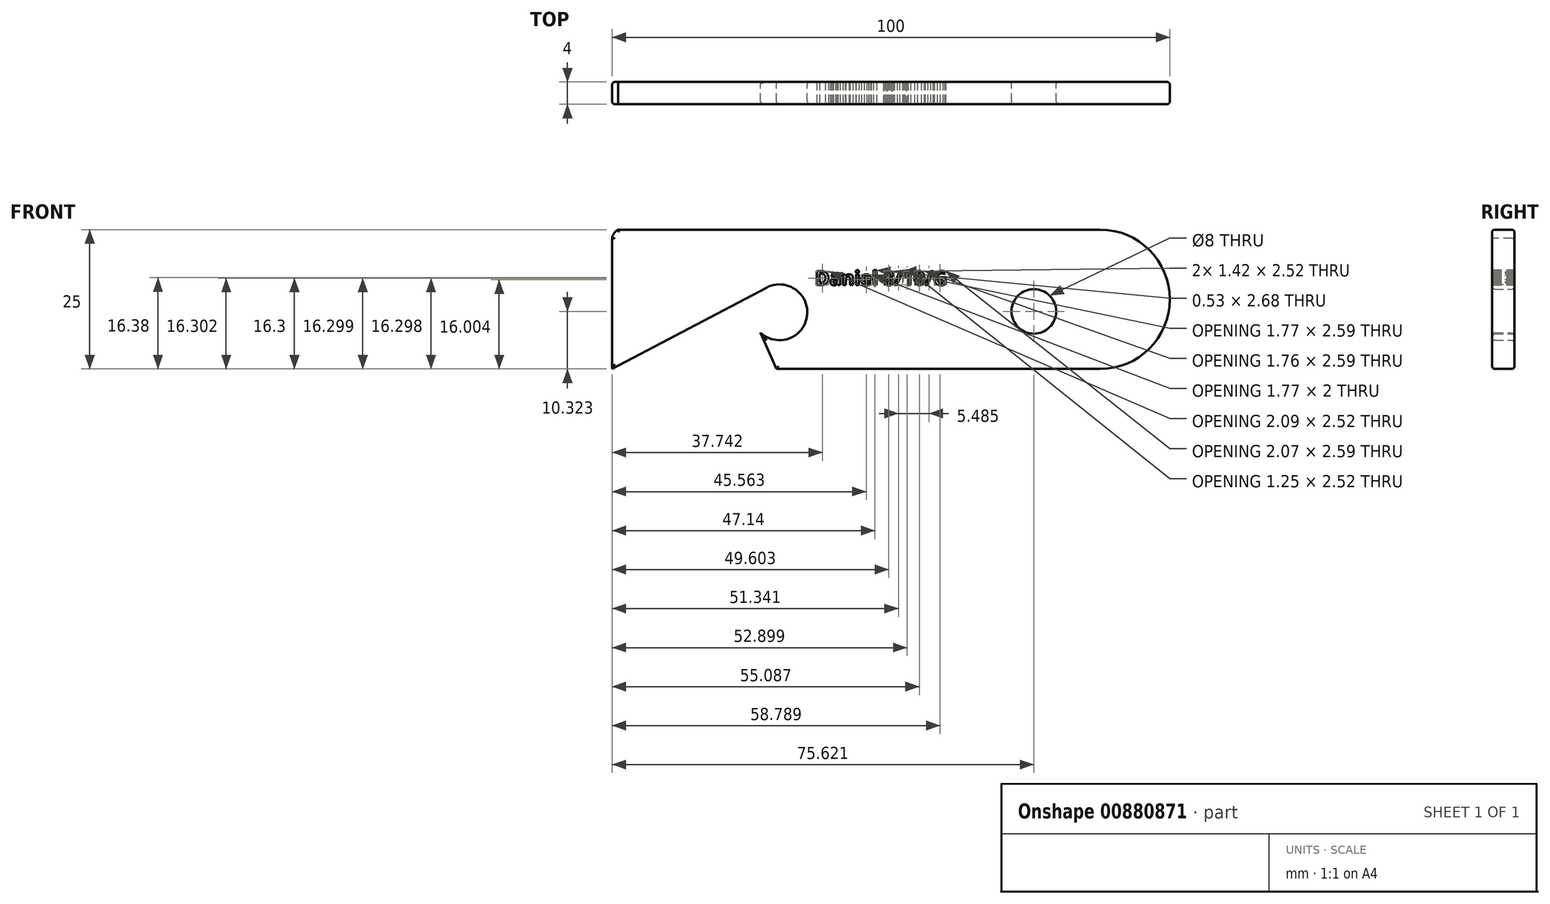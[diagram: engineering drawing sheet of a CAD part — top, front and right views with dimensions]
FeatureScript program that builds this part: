
annotation { "Feature Type Name" : "Feature", "Feature Type Description" : "" }
export const myFeature = defineFeature(function(context is Context, id is Id, definition is map)
    precondition{}
    {
        {
            var Q0;
            Q0=qCreatedBy(makeId("Front.planeOp"),FACE);
            var sketch = newSketch(context, id + "F0", { "sketchPlane" : qUnion([Q0])});
            skLineSegment(sketch, "E0.bottom", {"start": v(-60.03, 1.76) * mm, "end": v(39.97, 1.76) * mm});
            skLineSegment(sketch, "E0.top", {"start": v(-60.03, -23.24) * mm, "end": v(39.97, -23.24) * mm});
            skLineSegment(sketch, "E0.left", {"start": v(-60.03, 1.76) * mm, "end": v(-60.03, -23.24) * mm});
            skLineSegment(sketch, "E0.right", {"start": v(39.97, 1.76) * mm, "end": v(39.97, -23.24) * mm});
            skArc(sketch, "E1", {"start": v(27.47, -23.24) * mm, "mid": v(39.97, -10.74) * mm, "end": v(27.47, 1.76) * mm});
            skCircle(sketch, "E2", {"center": v(-30.03, -13.07) * mm, "radius": 5 * mm});
            skLineSegment(sketch, "E3", {"start": v(-60.03, -23.24) * mm, "end": v(-30.03, -7.42) * mm});
            skLineSegment(sketch, "E4", {"start": v(-33.46, -16.72) * mm, "end": v(-30.57, -23.24) * mm});
            skCircle(sketch, "E5", {"center": v(15.6, -12.92) * mm, "radius": 4 * mm});
            skSolve(sketch);
        }
        {
            var Q0;
            {var subQ5=sQuery(id+"F0.wireOp",EDGE,"E0.left");Q0=makeQuery(id+"F0.imprint","IMPRINT",FACE,{"disambiguationData":[TD([[makeQuery(id+"F0.imprint","IMPRINT",EDGE,{"derivedFrom":subQ5}),1.0]])]});}
            extrude(context, id + "F1", {"entities" : qUnion([Q0]), "depth" : 4 * mm, "offsetDistance" : 25 * mm});
        }
        {
            var Q0;
            Q0=makeQuery(id+"F1.opExtrude","CAP_FACE",FACE,{"disambiguationData":[OSD([sQuery(id+"F0.wireOp",EDGE,"E0.bottom"),sQuery(id+"F0.wireOp",EDGE,"E0.top"),sQuery(id+"F0.wireOp",EDGE,"E0.left"),sQuery(id+"F0.wireOp",EDGE,"E1"),sQuery(id+"F0.wireOp",EDGE,"E2"),sQuery(id+"F0.wireOp",EDGE,"E3"),sQuery(id+"F0.wireOp",EDGE,"E4"),sQuery(id+"F0.wireOp",EDGE,"17lc7Sft-6GVr-41g3-LSci-0BLGc6DZFp2w")])],"isStart":false});
            var sketch = newSketch(context, id + "F2", { "sketchPlane" : qUnion([Q0])});
            skArc(sketch, "E6", {"start": v(-58.94, 1.76) * mm, "mid": v(-59.68, 1.12) * mm, "end": v(-60.03, 0.2) * mm});
            skSolve(sketch);
        }
        {
            var Q0;
            {var subQ0=sQuery(id+"F2.wireOp",EDGE,"E6");Q0=makeQuery(id+"F2.imprint","IMPRINT",FACE,{"disambiguationData":[TD([[makeQuery(id+"F2.imprint","IMPRINT",EDGE,{"derivedFrom":subQ0}),-1.0]])]});}
            extrude(context, id + "F3", {"entities" : qUnion([Q0]), "operationType" : NewBodyOperationType.REMOVE, "endBound" : BoundingType.THROUGH_ALL, "oppositeDirection" : true, "depth" : 25 * mm, "offsetDistance" : 25 * mm});
        }
        {
            var Q0;
            Q0=makeQuery(id+"F1.opExtrude","CAP_FACE",FACE,{"disambiguationData":[OSD([sQuery(id+"F0.wireOp",EDGE,"E0.bottom"),sQuery(id+"F0.wireOp",EDGE,"E0.top"),sQuery(id+"F0.wireOp",EDGE,"E0.left"),sQuery(id+"F0.wireOp",EDGE,"E1"),sQuery(id+"F0.wireOp",EDGE,"E2"),sQuery(id+"F0.wireOp",EDGE,"E3"),sQuery(id+"F0.wireOp",EDGE,"E4"),sQuery(id+"F0.wireOp",EDGE,"E5")])],"isStart":false});
            fillet(context, id + "F4", {"entities" : qUnion([Q0]), "radius" : 0.5 * mm, "tangentPropagation" : true, "allowEdgeOverflow" : false});
        }
        {
            var Q0;
            Q0=makeQuery(id+"F1.opExtrude","CAP_FACE",FACE,{"disambiguationData":[OSD([sQuery(id+"F0.wireOp",EDGE,"E0.bottom"),sQuery(id+"F0.wireOp",EDGE,"E0.top"),sQuery(id+"F0.wireOp",EDGE,"E0.left"),sQuery(id+"F0.wireOp",EDGE,"E1"),sQuery(id+"F0.wireOp",EDGE,"E2"),sQuery(id+"F0.wireOp",EDGE,"E3"),sQuery(id+"F0.wireOp",EDGE,"E4"),sQuery(id+"F0.wireOp",EDGE,"E5")])],"isStart":true});
            fillet(context, id + "F5", {"entities" : qUnion([Q0]), "radius" : 0.5 * mm, "tangentPropagation" : true, "allowEdgeOverflow" : false});
        }
        {
            var Q0;
            Q0=makeQuery(id+"F1.opExtrude","CAP_FACE",FACE,{"disambiguationData":[OSD([sQuery(id+"F0.wireOp",EDGE,"E0.bottom"),sQuery(id+"F0.wireOp",EDGE,"E0.top"),sQuery(id+"F0.wireOp",EDGE,"E0.left"),sQuery(id+"F0.wireOp",EDGE,"E1"),sQuery(id+"F0.wireOp",EDGE,"E2"),sQuery(id+"F0.wireOp",EDGE,"E3"),sQuery(id+"F0.wireOp",EDGE,"E4"),sQuery(id+"F0.wireOp",EDGE,"E5")])],"isStart":false});
            var sketch = newSketch(context, id + "F6", { "sketchPlane" : qUnion([Q0])});
            skText(sketch, "E7", { "text": "Daniel 8/10/G", "fontName": "OpenSans-Bold.ttf"});
            const initialGuessF6  = {"E7": [-0.02365, -0.0082, 1, 0, 0.00254]};
            skSetInitialGuess(sketch, initialGuessF6);
            skSolve(sketch);
        }
        {
            var Q0;
            Q0 = qSketchRegion(id + "F6", true);
            extrude(context, id + "F7", {"entities" : qUnion([Q0]), "operationType" : NewBodyOperationType.REMOVE, "endBound" : BoundingType.THROUGH_ALL, "oppositeDirection" : true, "depth" : 25 * mm, "offsetDistance" : 25 * mm});
        }
    });
